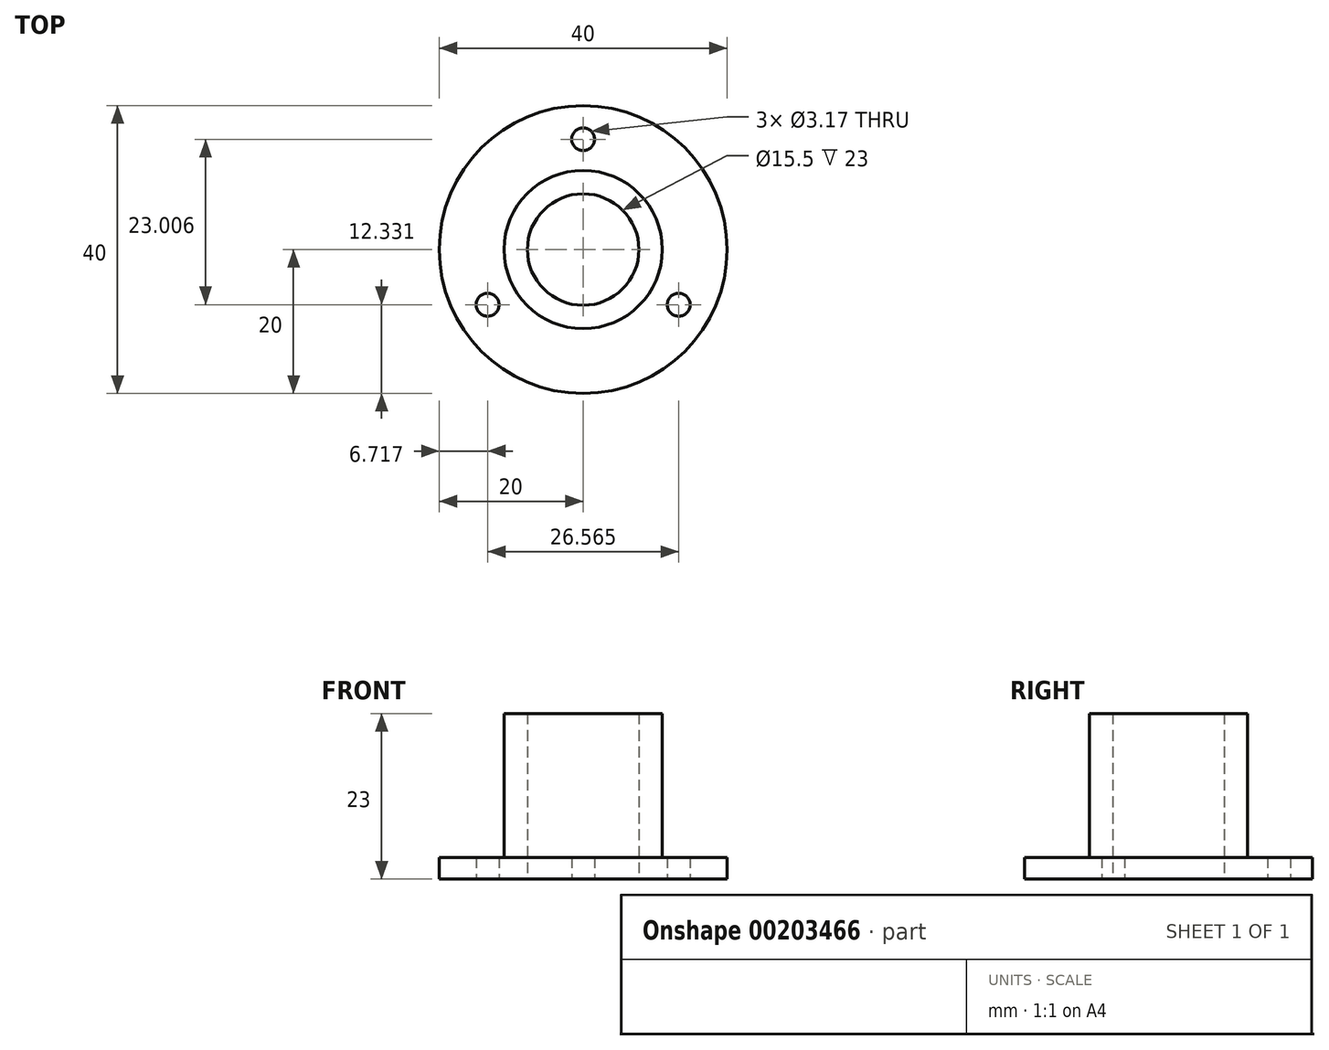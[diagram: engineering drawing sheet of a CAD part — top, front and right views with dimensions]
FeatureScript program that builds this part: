
annotation { "Feature Type Name" : "Feature", "Feature Type Description" : "" }
export const myFeature = defineFeature(function(context is Context, id is Id, definition is map)
    precondition{}
    {
        {
            var Q0;
            Q0=qCreatedBy(makeId("Top.planeOp"),FACE);
            var sketch = newSketch(context, id + "F0", { "sketchPlane" : qUnion([Q0])});
            skCircle(sketch, "E0", {"center": v(0, 0) * mm, "radius": 20 * mm});
            skCircle(sketch, "E1", {"center": v(0, 0) * mm, "radius": 11 * mm});
            skCircle(sketch, "E2", {"center": v(0, 0) * mm, "radius": 7.75 * mm});
            skCircle(sketch, "E3", {"center": v(0, 15.34) * mm, "radius": 1.59 * mm});
            skCircle(sketch, "E4.1.0", {"center": v(-13.28, -7.67) * mm, "radius": 1.59 * mm});
            skCircle(sketch, "E4.2.0", {"center": v(13.28, -7.67) * mm, "radius": 1.59 * mm});
            skSolve(sketch);
        }
        {
            var Q0;
            Q0=makeQuery(id+"F0.imprint","IMPRINT",FACE,{"disambiguationData":[TD([[makeQuery(id+"F0.imprint","IMPRINT",EDGE,{"derivedFrom":sQuery(id+"F0.wireOp",EDGE,"E1")}),1.0]])]});
            extrude(context, id + "F1", {"entities" : qUnion([Q0]), "depth" : 23 * mm});
        }
        {
            var Q0;
            Q0 = qSketchRegion(id + "F0", true);
            extrude(context, id + "F2", {"entities" : qUnion([Q0]), "operationType" : NewBodyOperationType.ADD, "depth" : 3 * mm});
        }
    });
